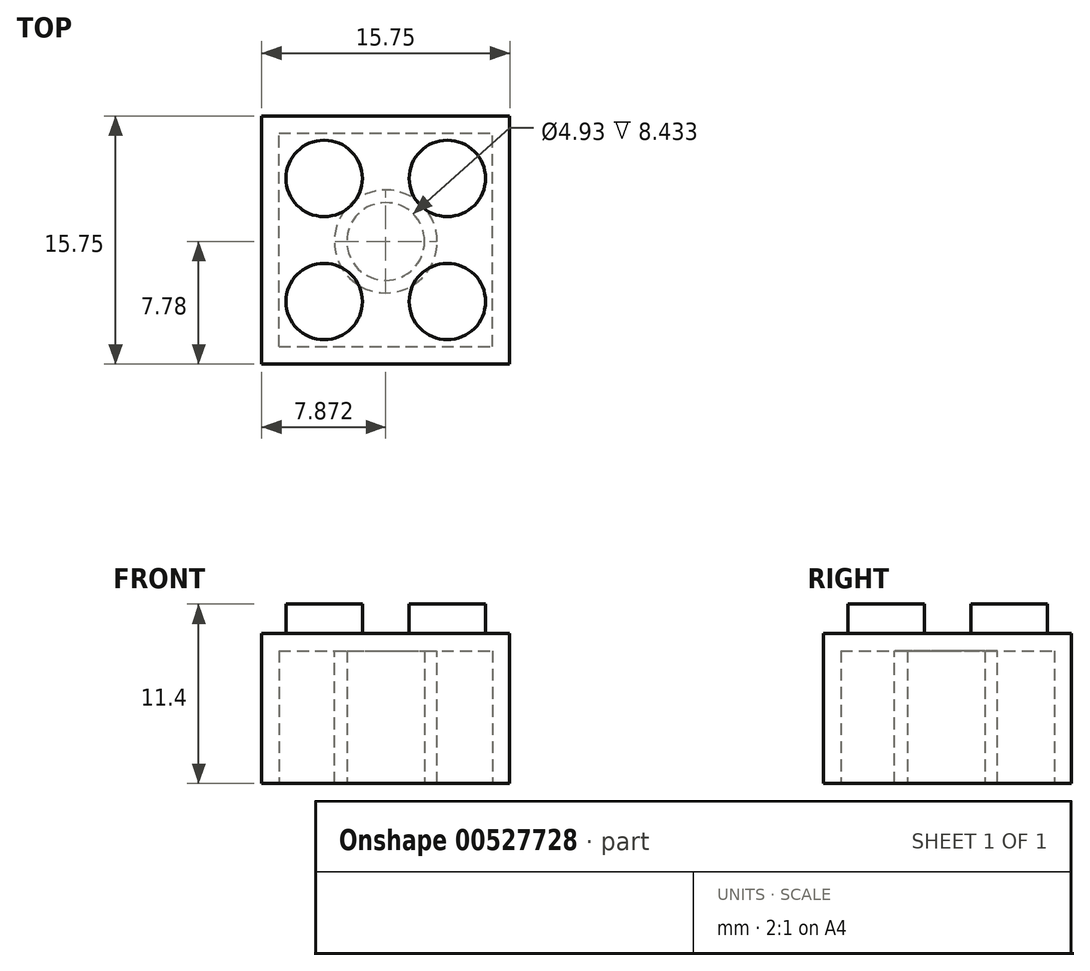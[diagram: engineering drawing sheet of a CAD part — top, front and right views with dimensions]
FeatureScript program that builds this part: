
annotation { "Feature Type Name" : "Feature", "Feature Type Description" : "" }
export const myFeature = defineFeature(function(context is Context, id is Id, definition is map)
    precondition{}
    {
        {
            var Q0;
            Q0=qCreatedBy(makeId("Top.planeOp"),FACE);
            var sketch = newSketch(context, id + "F0", { "sketchPlane" : qUnion([Q0])});
            skLineSegment(sketch, "E0.bottom", {"start": v(-7.44, 7.97) * mm, "end": v(8.3, 7.97) * mm});
            skLineSegment(sketch, "E0.top", {"start": v(-7.44, -7.78) * mm, "end": v(8.3, -7.78) * mm});
            skLineSegment(sketch, "E0.left", {"start": v(-7.44, 7.97) * mm, "end": v(-7.44, -7.78) * mm});
            skLineSegment(sketch, "E0.right", {"start": v(8.3, 7.97) * mm, "end": v(8.3, -7.78) * mm});
            skSolve(sketch);
        }
        {
            var Q0;
            Q0 = qSketchRegion(id + "F0", true);
            extrude(context, id + "F1", {"entities" : qUnion([Q0]), "depth" : 9.52 * mm, "offsetDistance" : 25.4 * mm});
        }
        {
            var Q0;
            Q0=makeQuery(id+"F1.opExtrude","CAP_FACE",FACE,{"disambiguationData":[OSD([sQuery(id+"F0.wireOp",EDGE,"E0.bottom"),sQuery(id+"F0.wireOp",EDGE,"E0.top"),sQuery(id+"F0.wireOp",EDGE,"E0.left"),sQuery(id+"F0.wireOp",EDGE,"E0.right")])],"isStart":false});
            var sketch = newSketch(context, id + "F2", { "sketchPlane" : qUnion([Q0])});
            skCircle(sketch, "E1", {"center": v(-3.48, 4) * mm, "radius": 2.43 * mm});
            skCircle(sketch, "E2", {"center": v(4.34, 4) * mm, "radius": 2.43 * mm});
            skCircle(sketch, "E3", {"center": v(-3.48, -3.81) * mm, "radius": 2.43 * mm});
            skCircle(sketch, "E4", {"center": v(4.34, -3.81) * mm, "radius": 2.43 * mm});
            skSolve(sketch);
        }
        {
            var Q0;
            Q0 = qSketchRegion(id + "F2", true);
            extrude(context, id + "F3", {"entities" : qUnion([Q0]), "operationType" : NewBodyOperationType.ADD, "depth" : 1.88 * mm, "offsetDistance" : 25.4 * mm});
        }
        {
            var Q0;
            Q0=makeQuery(id+"F1.opExtrude","CAP_FACE",FACE,{"disambiguationData":[OSD([sQuery(id+"F0.wireOp",EDGE,"E0.bottom"),sQuery(id+"F0.wireOp",EDGE,"E0.top"),sQuery(id+"F0.wireOp",EDGE,"E0.left"),sQuery(id+"F0.wireOp",EDGE,"E0.right")])],"isStart":true});
            var sketch = newSketch(context, id + "F4", { "sketchPlane" : qUnion([Q0])});
            skLineSegment(sketch, "E5.bottom", {"start": v(-6.35, 6.68) * mm, "end": v(7.21, 6.68) * mm});
            skLineSegment(sketch, "E5.top", {"start": v(-6.35, -6.88) * mm, "end": v(7.21, -6.88) * mm});
            skLineSegment(sketch, "E5.left", {"start": v(-6.35, 6.68) * mm, "end": v(-6.35, -6.88) * mm});
            skLineSegment(sketch, "E5.right", {"start": v(7.21, 6.68) * mm, "end": v(7.21, -6.88) * mm});
            skSolve(sketch);
        }
        {
            var Q0;
            Q0 = qSketchRegion(id + "F4", true);
            extrude(context, id + "F5", {"entities" : qUnion([Q0]), "operationType" : NewBodyOperationType.REMOVE, "oppositeDirection" : true, "depth" : 8.43 * mm, "offsetDistance" : 25.4 * mm});
        }
        {
            var Q0;
            Q0=makeQuery(id+"F5.boolean.opBoolean","COPY",FACE,{"derivedFrom":makeQuery(id+"F5.opExtrude","CAP_FACE",FACE,{"disambiguationData":[OSD([sQuery(id+"F4.wireOp",EDGE,"E5.bottom"),sQuery(id+"F4.wireOp",EDGE,"E5.top"),sQuery(id+"F4.wireOp",EDGE,"E5.left"),sQuery(id+"F4.wireOp",EDGE,"E5.right")])],"isStart":false})});
            var sketch = newSketch(context, id + "F6", { "sketchPlane" : qUnion([Q0])});
            skCircle(sketch, "E6", {"center": v(0.43, 0) * mm, "radius": 3.27 * mm});
            skSolve(sketch);
        }
        {
            var Q0;
            Q0 = qSketchRegion(id + "F6", true);
            extrude(context, id + "F7", {"entities" : qUnion([Q0]), "operationType" : NewBodyOperationType.ADD, "depth" : 8.43 * mm, "offsetDistance" : 25.4 * mm});
        }
        {
            var Q0;
            Q0=makeQuery(id+"F7.opExtrude","CAP_FACE",FACE,{"disambiguationData":[OSD([sQuery(id+"F6.wireOp",EDGE,"E6")])],"isStart":false});
            var sketch = newSketch(context, id + "F8", { "sketchPlane" : qUnion([Q0])});
            skCircle(sketch, "E7", {"center": v(0.43, 0) * mm, "radius": 2.47 * mm});
            skSolve(sketch);
        }
        {
            var Q0;
            Q0=makeQuery(id+"F8.imprint","IMPRINT",FACE,{"disambiguationData":[TD([[makeQuery(id+"F8.imprint","IMPRINT",EDGE,{"derivedFrom":sQuery(id+"F8.wireOp",EDGE,"E7")}),1.0]])]});
            extrude(context, id + "F9", {"entities" : qUnion([Q0]), "operationType" : NewBodyOperationType.REMOVE, "oppositeDirection" : true, "depth" : 8.43 * mm, "offsetDistance" : 25.4 * mm});
        }
    });
